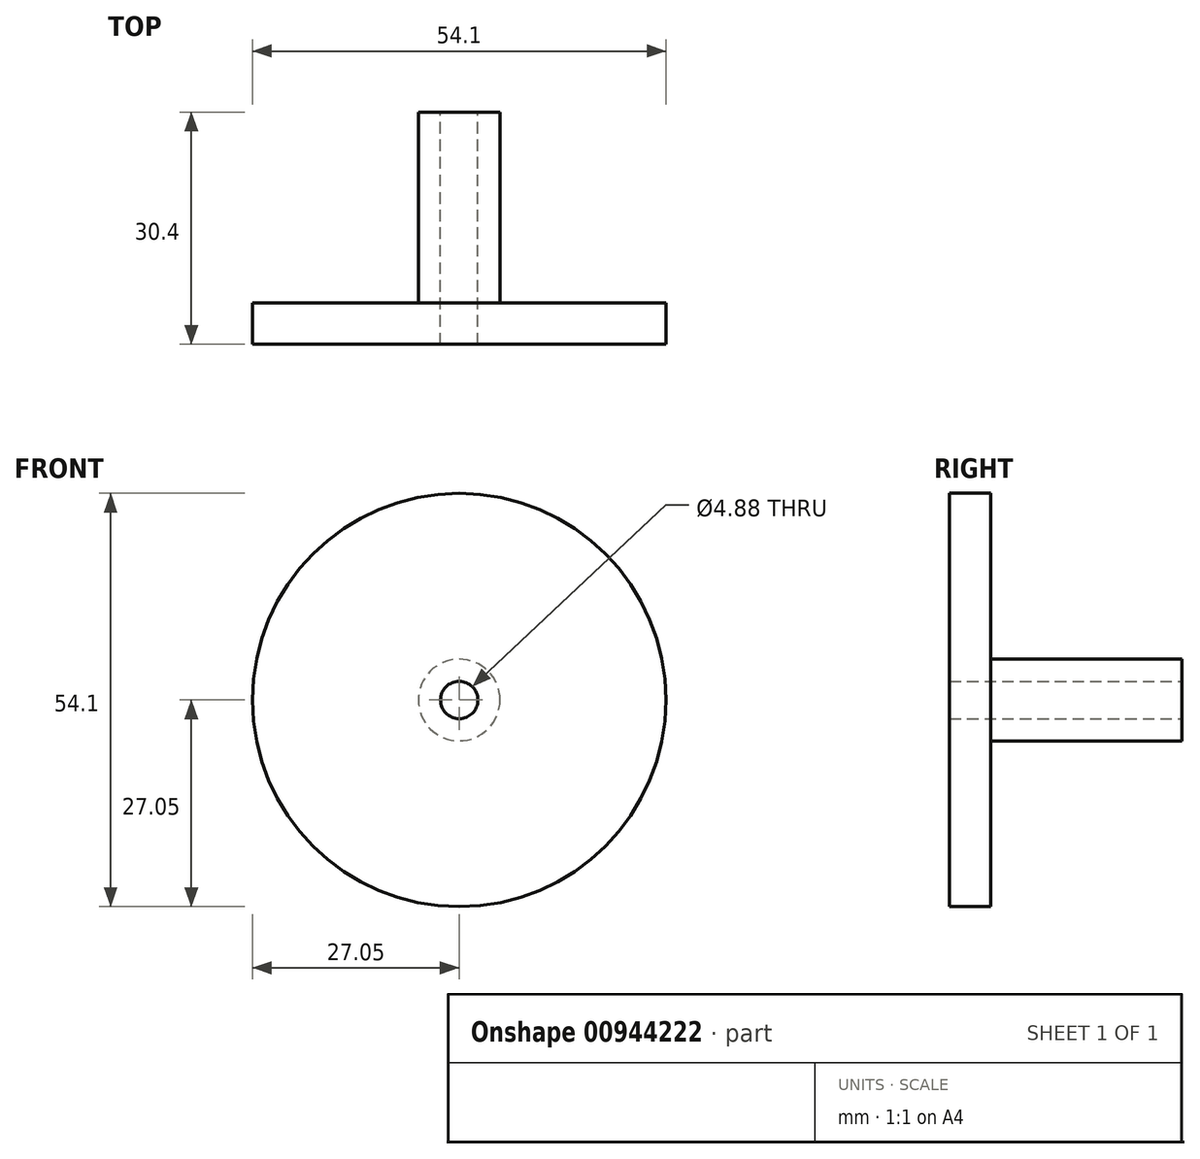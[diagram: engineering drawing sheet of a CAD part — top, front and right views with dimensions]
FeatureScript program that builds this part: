
annotation { "Feature Type Name" : "Feature", "Feature Type Description" : "" }
export const myFeature = defineFeature(function(context is Context, id is Id, definition is map)
    precondition{}
    {
        {
            var Q0;
            Q0=qCreatedBy(makeId("Front.planeOp"),FACE);
            var sketch = newSketch(context, id + "F0", { "sketchPlane" : qUnion([Q0])});
            skCircle(sketch, "E0", {"center": v(0, 0) * mm, "radius": 27.05 * mm});
            skSolve(sketch);
        }
        {
            var Q0;
            Q0 = qSketchRegion(id + "F0", true);
            extrude(context, id + "F1", {"entities" : qUnion([Q0]), "depth" : 5.4 * mm, "offsetDistance" : 25 * mm});
        }
        {
            var Q0;
            Q0=makeQuery(id+"F1.opExtrude","CAP_FACE",FACE,{"disambiguationData":[OSD([sQuery(id+"F0.wireOp",EDGE,"E0")])],"isStart":true});
            var sketch = newSketch(context, id + "F2", { "sketchPlane" : qUnion([Q0])});
            skCircle(sketch, "E1", {"center": v(0, 0) * mm, "radius": 5.34 * mm});
            skSolve(sketch);
        }
        {
            var Q0;
            Q0 = qSketchRegion(id + "F2", true);
            extrude(context, id + "F3", {"entities" : qUnion([Q0]), "operationType" : NewBodyOperationType.ADD, "depth" : 25 * mm, "offsetDistance" : 25 * mm});
        }
        {
            var Q0;
            Q0=makeQuery(id+"F3.opExtrude","CAP_FACE",FACE,{"disambiguationData":[OSD([sQuery(id+"F2.wireOp",EDGE,"E1")])],"isStart":false});
            var sketch = newSketch(context, id + "F4", { "sketchPlane" : qUnion([Q0])});
            skCircle(sketch, "E2", {"center": v(0, 0) * mm, "radius": 2.44 * mm});
            skSolve(sketch);
        }
        {
            var Q0;
            Q0=makeQuery(id+"F4.imprint","IMPRINT",FACE,{"disambiguationData":[TD([[makeQuery(id+"F4.imprint","IMPRINT",EDGE,{"derivedFrom":sQuery(id+"F4.wireOp",EDGE,"E2")}),1.0]])]});
            var Q1;
            Q1=sQuery(id+"F4.wireOp",EDGE,"E2");
            extrude(context, id + "F5", {"entities" : qUnion([Q0]), "operationType" : NewBodyOperationType.REMOVE, "surfaceOperationType" : NewSurfaceOperationType.ADD, "surfaceEntities" : qUnion([Q1]), "endBound" : BoundingType.SYMMETRIC, "oppositeDirection" : true, "depth" : 97.6 * mm, "offsetDistance" : 25 * mm});
        }
    });
